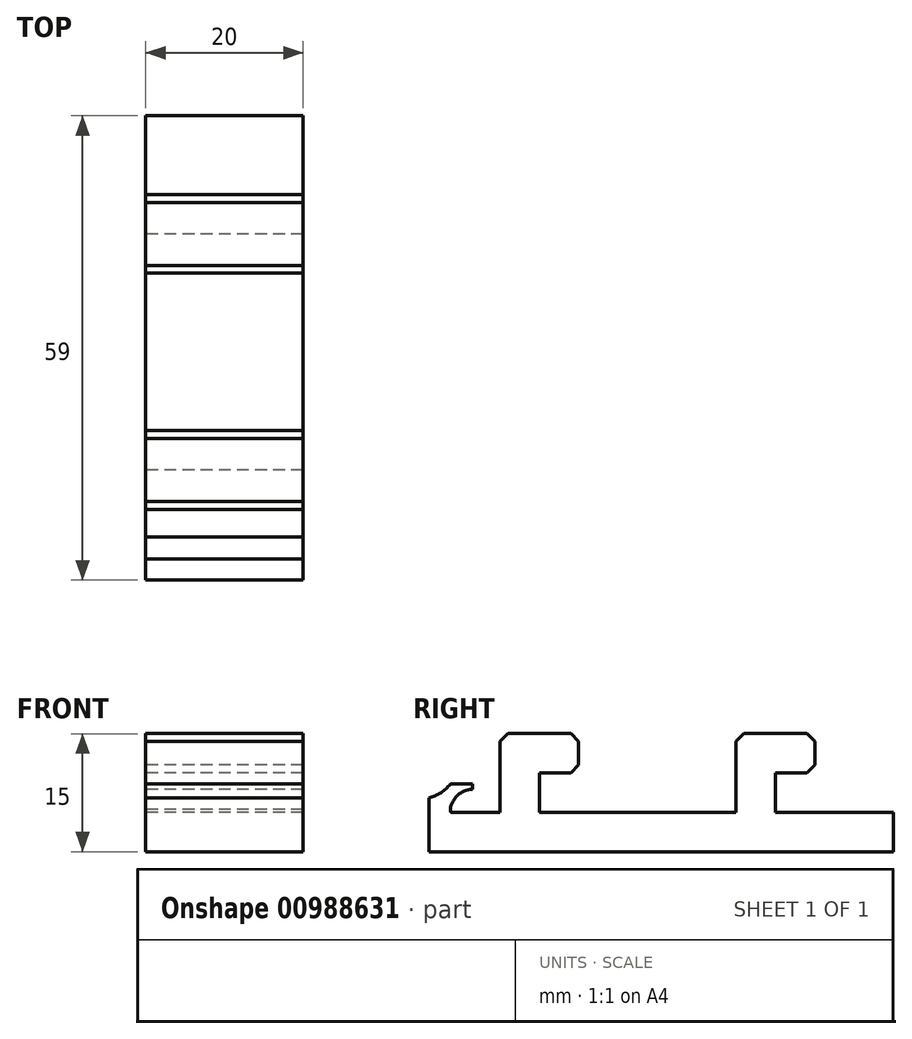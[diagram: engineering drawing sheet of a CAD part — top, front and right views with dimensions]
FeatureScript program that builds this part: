
annotation { "Feature Type Name" : "Feature", "Feature Type Description" : "" }
export const myFeature = defineFeature(function(context is Context, id is Id, definition is map)
    precondition{}
    {
        {
            var Q0;
            Q0=qCreatedBy(makeId("Right.planeOp"),FACE);
            var sketch = newSketch(context, id + "F0", { "sketchPlane" : qUnion([Q0])});
            skLineSegment(sketch, "E0.bottom", {"start": v(2.7, 2.31) * mm, "end": v(5.5, 2.31) * mm});
            skLineSegment(sketch, "E0.right", {"start": v(5.5, 2.31) * mm, "end": v(5.5, 1.65) * mm});
            skLineSegment(sketch, "E1", {"start": v(2.7, -1.07) * mm, "end": v(2.7, -0.9) * mm});
            skLineSegment(sketch, "E2.top", {"start": v(0, -6.29) * mm, "end": v(9, -6.29) * mm});
            skLineSegment(sketch, "E2.right", {"start": v(9, -1.29) * mm, "end": v(9, -6.29) * mm});
            skLineSegment(sketch, "E3", {"start": v(2.92, -1.29) * mm, "end": v(9, -1.29) * mm});
            skArc(sketch, "E4", {"start": v(0, 0.58) * mm, "mid": v(1.5, 1.2) * mm, "end": v(2.7, 2.31) * mm});
            skPoint(sketch, "E5.visualSharp", {"position": v(2.7, -1.29) * mm});
            skArc(sketch, "E5.filletArc", {"start": v(2.7, -1.07) * mm, "mid": v(2.76, -1.22) * mm, "end": v(2.92, -1.29) * mm});
            skArc(sketch, "E6", {"start": v(5.5, 1.65) * mm, "mid": v(3.63, 0.89) * mm, "end": v(2.7, -0.9) * mm});
            skLineSegment(sketch, "E7", {"start": v(0, 0.58) * mm, "end": v(0, -6.29) * mm});
            skLineSegment(sketch, "E8", {"start": v(2.7, -0.9) * mm, "end": v(2.7, 6.55) * mm, "construction": true});
            skSolve(sketch);
        }
        {
            var Q0;
            Q0=qSketchRegion(id+"F0",true);
            extrude(context, id + "F1", {"entities" : qUnion([Q0]), "depth" : 20 * mm, "offsetDistance" : 25.4 * mm});
        }
        {
            var Q0;
            Q0=qCreatedBy(makeId("Right.planeOp"),FACE);
            var sketch = newSketch(context, id + "F2", { "sketchPlane" : qUnion([Q0])});
            skLineSegment(sketch, "E9.bottom", {"start": v(9, -6.29) * mm, "end": v(59, -6.29) * mm});
            skLineSegment(sketch, "E9.top", {"start": v(9, 8.71) * mm, "end": v(19, 8.71) * mm});
            skLineSegment(sketch, "E9.left", {"start": v(9, -6.29) * mm, "end": v(9, 8.71) * mm});
            skLineSegment(sketch, "E9.right", {"start": v(59, -6.29) * mm, "end": v(59, -1.29) * mm});
            skLineSegment(sketch, "E10.left", {"start": v(19, 8.71) * mm, "end": v(19, 3.71) * mm});
            skLineSegment(sketch, "E11.bottom", {"start": v(19, 3.71) * mm, "end": v(14, 3.71) * mm});
            skLineSegment(sketch, "E11.top", {"start": v(39, -1.29) * mm, "end": v(14, -1.29) * mm});
            skLineSegment(sketch, "E11.right", {"start": v(14, 3.71) * mm, "end": v(14, -1.29) * mm});
            skLineSegment(sketch, "E12", {"start": v(49, 8.71) * mm, "end": v(49, 3.71) * mm});
            skLineSegment(sketch, "E13", {"start": v(49, 3.71) * mm, "end": v(44, 3.71) * mm});
            skLineSegment(sketch, "E14", {"start": v(44, 3.71) * mm, "end": v(44, -1.29) * mm});
            skLineSegment(sketch, "E15", {"start": v(44, -1.29) * mm, "end": v(59, -1.29) * mm});
            skLineSegment(sketch, "E16", {"start": v(39, -1.29) * mm, "end": v(39, 8.71) * mm});
            skLineSegment(sketch, "E17.trimOffspring", {"start": v(39, 8.71) * mm, "end": v(49, 8.71) * mm});
            skSolve(sketch);
        }
        {
            var Q0;
            Q0 = qSketchRegion(id + "F2", true);
            extrude(context, id + "F3", {"entities" : qUnion([Q0]), "operationType" : NewBodyOperationType.ADD, "depth" : 20 * mm, "offsetDistance" : 25.4 * mm});
        }
        {
            var Q0;
            Q0=makeQuery(id+"F3.opExtrude","SWEPT_EDGE",EDGE,{"disambiguationData":[OSD([sQuery(id+"F2.wireOp",EDGE,"E10.left"),sQuery(id+"F2.wireOp",EDGE,"E11.bottom")])]});
            var Q1;
            Q1=makeQuery(id+"F3.opExtrude","SWEPT_EDGE",EDGE,{"disambiguationData":[OSD([sQuery(id+"F2.wireOp",EDGE,"E9.top"),sQuery(id+"F2.wireOp",EDGE,"E10.left")])]});
            var Q2;
            Q2=makeQuery(id+"F3.opExtrude","SWEPT_EDGE",EDGE,{"disambiguationData":[OSD([sQuery(id+"F2.wireOp",EDGE,"E12"),sQuery(id+"F2.wireOp",EDGE,"E17.trimOffspring")])]});
            var Q3;
            Q3=makeQuery(id+"F3.opExtrude","SWEPT_EDGE",EDGE,{"disambiguationData":[OSD([sQuery(id+"F2.wireOp",EDGE,"E12"),sQuery(id+"F2.wireOp",EDGE,"E13")])]});
            var Q4;
            Q4=makeQuery(id+"F3.opExtrude","SWEPT_EDGE",EDGE,{"disambiguationData":[OSD([sQuery(id+"F2.wireOp",EDGE,"E16"),sQuery(id+"F2.wireOp",EDGE,"E17.trimOffspring")])]});
            var Q5;
            Q5=makeQuery(id+"F3.opExtrude","SWEPT_EDGE",EDGE,{"disambiguationData":[OSD([sQuery(id+"F2.wireOp",EDGE,"E9.top"),sQuery(id+"F2.wireOp",EDGE,"E9.left")])]});
            chamfer(context, id + "F4", {"entities" : qUnion([Q0, Q1, Q2, Q3, Q4, Q5]), "width" : 1 * mm, "tangentPropagation" : true});
        }
    });
